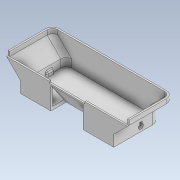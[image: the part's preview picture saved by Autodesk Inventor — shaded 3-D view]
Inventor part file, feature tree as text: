
AUTODESK INVENTOR PART (.ipt)
format: ipt  version: 2022.1 (Build 261234020, 234B)  size: 344,064 bytes
history: native  units: mm
features: reference x16, sketch x14, extrude x9, other x7, projected_geometry x5, plane x3, hole x3, loft x2, chamfer x2, fillet x2, direct_edit x1, move_body x1
ambient origin geometry x8: Origin, YZ Plane, XZ Plane, XY Plane, X Axis, Y Axis, Z Axis, Center Point
bodies: Volumenkörper1 (feature_tree)
feature tree (65):
  extrude  "Extrusion1"  Depth=0.3mm
  plane  "Arbeitsebene1"
  plane  "Arbeitsebene2"
  sketch  "Skizze4"  dims[d4=2.0mm d5=2.0mm]
  sketch  "Skizze3"  dims[d2=0.3mm d3=2.0mm]
  loft  "Erhebung1"
  loft  "Erhebung2"
  direct_edit  "Direktbearbeitung1"
  extrude  "Extrusion3"  Depth=2.0mm
  sketch  "Skizze6"  dims[d10=81.000047mm d11=93.000047mm]
  extrude  "Extrusion4"  Depth=93.000047mm
  extrude  "Extrusion5"  Depth=2.0mm TaperAngle=0.0deg
  sketch  "Skizze10"  dims[d31=0.0mm d32=90.0deg d33=0.0mm d34=90.0deg d35=0.0mm d36=90.0deg]
  hole  "Bohrung2"  [1 undecoded]
  hole  "Bohrung3"  [1 undecoded]
  chamfer  "Fase1"  Angle=90.0deg  [1 undecoded]
  fillet  "Rundung1"  Radius=2.0mm
  fillet  "Rundung2"  Radius=5.65mm
  extrude  "Extrusion6"  Depth=2.0mm
  extrude  "Extrusion7"  Depth=2.0mm
  chamfer  "Fase2"  Distance=5.6mm
  hole  "Bohrung4"  [1 undecoded]
  plane  "Arbeitsebene3"
  extrude  "Extrusion10"  Depth=40.0mm
  extrude  "Extrusion11"  Depth=1.9999mm
  extrude  "Extrusion12"  Depth=40.0mm
  sketch  "Skizze1"  dims[d0=0.3mm d1=0.3mm]
  reference  "Referenz1"
  reference  "Referenz2"
  reference  "Referenz3"
  reference  "Referenz4"
  reference  "Referenz5"
  reference  "Referenz6"
  reference  "Referenz7"
  reference  "Referenz8"
  reference  "Referenz9"
  reference  "Referenz10"
  projected_geometry  "Projizierte Kontur2"
  projected_geometry  "Projizierte Kontur3"
  sketch  "Skizze5"  dims[d7=0.3mm d9=2.0mm]
  projected_geometry  "Projizierte Kontur4"
  reference  "Referenz11"
  sketch  "Skizze7"  dims[d12=2.0mm d13=13.6mm d14=0.0mm]
  projected_geometry  "Projizierte Kontur5"
  sketch  "Skizze8"  dims[d15=17.0mm d29=0.0mm d30=90.0deg]
  sketch  "Skizze11"  dims[d37=0.0mm d38=0.0mm d39=0.4mm d40=2.0mm d41=5.65mm d42=0.0mm]
  sketch  "Skizze12"  dims[d43=4.0mm d44=0.0mm d45=2.0mm]
  sketch  "Skizze13"  dims[d47=2.0mm d48=2.0mm]
  reference  "Referenz12"
  reference  "Referenz13"
  reference  "Referenz14"
  reference  "Referenz15"
  sketch  "Skizze16"  dims[d49=2.0mm d50=5.6mm d51=0.0mm]
  sketch  "Skizze17"  dims[d59=6.0mm d60=6.0mm d61=4.0mm d62=2.0mm d63=90.0deg d64=3.2mm d65=0.0mm]
  projected_geometry  "Projizierte Kontur6"
  sketch  "Skizze18"  dims[d66=6.0mm d67=6.0mm d68=4.0mm d69=2.0mm d70=90.0deg d71=3.2mm d72=0.0mm d73=1.0mm d74=2.0mm d75=45.0deg d76=3.0mm d77=1.9999mm d78=3.0mm d79=5.6mm d80=0.0mm d81=3.0mm d82=10.0mm d83=0.0mm d84=2.0mm d85=2.0mm d86=45.0deg d87=6.12mm d88=6.0mm d89=4.0mm d90=2.0mm d91=90.0deg d92=3.2mm d93=0.0mm d102=6.108652mm d103=19.0mm d104=40.0mm d105=0.0mm d106=2.0mm d107=40.0mm d108=0.0mm d109=3.0mm d110=3.0mm d111=6.0mm d112=0.0mm d113=1.0mm d114=1.0mm d115=1.0mm d116=0.15mm d117=6.0mm d118=0.375mm d119=14.3117mm d120=0.75mm d121=20.594885mm d122=0.0625mm d123=0.75mm d124=0.375mm]
  reference  "Referenz16"
  other  "<userpath>\Desktop\RAMA_SBNG\BedPan\Ramabed.iam"
  other  "Ramabed.iam"
  other  "Ramabed Cover:1"
  move_body  "Verschieben1"
  other  "Ramabed wago mount:1"
  other  "<userpath>\Desktop\RAMA_SBNG\BedPan\BucketR.iam"
  other  "BucketR.iam"
  other  "Brush_Holder:1"
note: 4 required parameter values undecoded (feature->parameter linkage not recoverable at this tier; creation-order binding heuristic only, values carry confidence <= 0.55)
